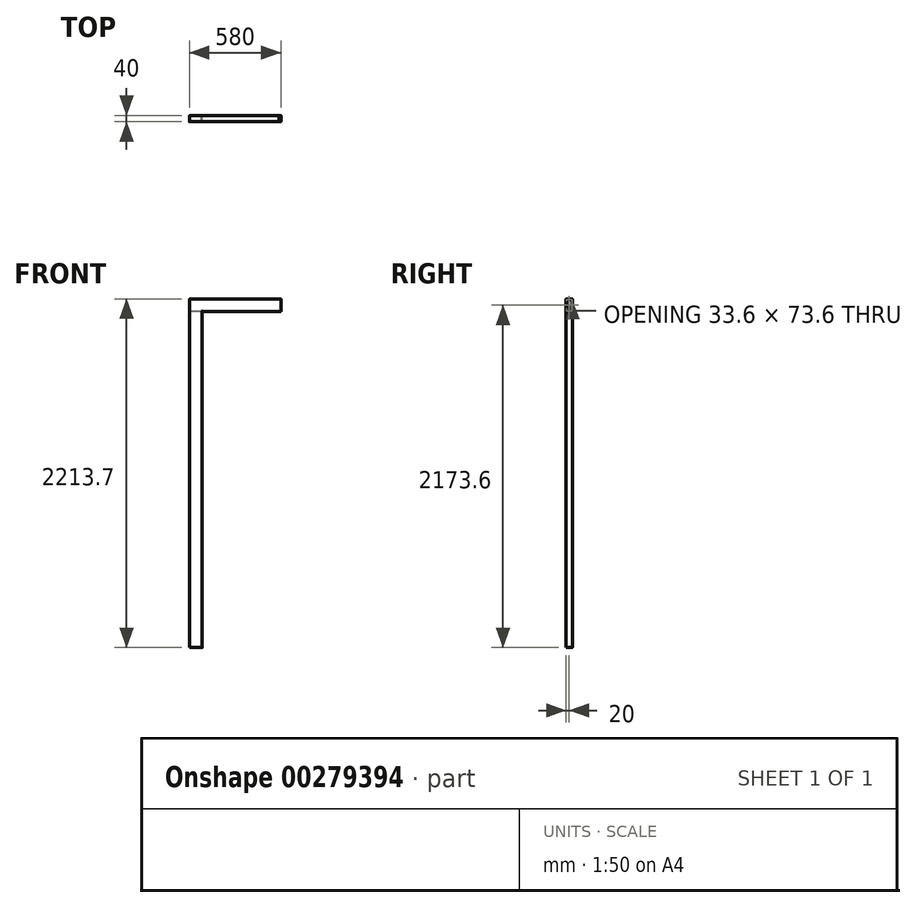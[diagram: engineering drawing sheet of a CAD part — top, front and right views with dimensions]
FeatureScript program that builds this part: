
annotation { "Feature Type Name" : "Feature", "Feature Type Description" : "" }
export const myFeature = defineFeature(function(context is Context, id is Id, definition is map)
    precondition{}
    {
        {
            var Q0;
            Q0=qCreatedBy(makeId("Top.planeOp"),FACE);
            var sketch = newSketch(context, id + "F0", { "sketchPlane" : qUnion([Q0])});
            skLineSegment(sketch, "E0.bottom", {"start": v(40, -20) * mm, "end": v(-40, -20) * mm});
            skLineSegment(sketch, "E0.top", {"start": v(40, 20) * mm, "end": v(-40, 20) * mm});
            skLineSegment(sketch, "E0.left", {"start": v(40, -20) * mm, "end": v(40, 20) * mm});
            skLineSegment(sketch, "E0.right", {"start": v(-40, -20) * mm, "end": v(-40, 20) * mm});
            skPoint(sketch, "E0.middle", {"position": v(0, 0) * mm});
            skLineSegment(sketch, "E1.bottom", {"start": v(34.8, -16.8) * mm, "end": v(-34.8, -16.8) * mm});
            skLineSegment(sketch, "E1.top", {"start": v(34.8, 16.8) * mm, "end": v(-34.8, 16.8) * mm});
            skLineSegment(sketch, "E1.left", {"start": v(36.8, -14.8) * mm, "end": v(36.8, 14.8) * mm});
            skLineSegment(sketch, "E1.right", {"start": v(-36.8, -14.8) * mm, "end": v(-36.8, 14.8) * mm});
            skPoint(sketch, "E2.visualSharp", {"position": v(-36.8, -16.8) * mm});
            skArc(sketch, "E2.filletArc", {"start": v(-36.8, -14.8) * mm, "mid": v(-36.21, -16.21) * mm, "end": v(-34.8, -16.8) * mm});
            skPoint(sketch, "E3.visualSharp", {"position": v(36.8, 16.8) * mm});
            skArc(sketch, "E3.filletArc", {"start": v(36.8, 14.8) * mm, "mid": v(36.21, 16.21) * mm, "end": v(34.8, 16.8) * mm});
            skPoint(sketch, "E4.visualSharp", {"position": v(36.8, -16.8) * mm});
            skArc(sketch, "E4.filletArc", {"start": v(34.8, -16.8) * mm, "mid": v(36.21, -16.21) * mm, "end": v(36.8, -14.8) * mm});
            skPoint(sketch, "E5.visualSharp", {"position": v(-36.8, 16.8) * mm});
            skArc(sketch, "E5.filletArc", {"start": v(-34.8, 16.8) * mm, "mid": v(-36.21, 16.21) * mm, "end": v(-36.8, 14.8) * mm});
            skSolve(sketch);
        }
        {
            var Q0;
            Q0=makeQuery(id+"F0.imprint","IMPRINT",FACE,{"disambiguationData":[TD([[makeQuery(id+"F0.imprint","IMPRINT",EDGE,{"derivedFrom":sQuery(id+"F0.wireOp",EDGE,"E0.bottom")}),-1.0]])]});
            extrude(context, id + "F1", {"entities" : qUnion([Q0]), "depth" : 2133.6 * mm});
        }
        {
            var Q0;
            Q0=makeQuery(id+"F1.opExtrude","CAP_FACE",FACE,{"disambiguationData":[OSD([sQuery(id+"F0.wireOp",EDGE,"E0.bottom"),sQuery(id+"F0.wireOp",EDGE,"E0.top"),sQuery(id+"F0.wireOp",EDGE,"E0.left"),sQuery(id+"F0.wireOp",EDGE,"E0.right"),sQuery(id+"F0.wireOp",EDGE,"E1.bottom"),sQuery(id+"F0.wireOp",EDGE,"E1.top"),sQuery(id+"F0.wireOp",EDGE,"E1.left"),sQuery(id+"F0.wireOp",EDGE,"E1.right"),sQuery(id+"F0.wireOp",EDGE,"E2.filletArc"),sQuery(id+"F0.wireOp",EDGE,"E3.filletArc"),sQuery(id+"F0.wireOp",EDGE,"E4.filletArc"),sQuery(id+"F0.wireOp",EDGE,"E5.filletArc")])],"isStart":false});
            var sketch = newSketch(context, id + "F2", { "sketchPlane" : qUnion([Q0])});
            skLineSegment(sketch, "E6.bottom", {"start": v(-40, -20) * mm, "end": v(40, -20) * mm});
            skLineSegment(sketch, "E6.top", {"start": v(-40, 20) * mm, "end": v(40, 20) * mm});
            skLineSegment(sketch, "E6.left", {"start": v(-40, -20) * mm, "end": v(-40, 20) * mm});
            skLineSegment(sketch, "E6.right", {"start": v(40, -20) * mm, "end": v(40, 20) * mm});
            skSolve(sketch);
        }
        {
            var Q0;
            Q0 = qSketchRegion(id + "F2", true);
            extrude(context, id + "F3", {"entities" : qUnion([Q0]), "operationType" : NewBodyOperationType.ADD, "depth" : 80 * mm});
        }
        {
            var Q0;
            {var subQ0=sQuery(id+"F0.wireOp",EDGE,"E0.left");Q0=makeQuery(id+"F3.boolean.opBoolean","MERGE",FACE,{"derivedFrom":[makeQuery(id+"F1q7NHaxA0HExfM_1.boolean.opBoolean","MERGE",FACE,{"derivedFrom":[makeQuery(id+"F1.opExtrude","SWEPT_FACE",FACE,{"disambiguationData":[OSD([subQ0])]}),makeQuery(id+"F1q7NHaxA0HExfM_1.opExtrude","SWEPT_FACE",FACE,{"disambiguationData":[OSD([subQ0])]})]}),makeQuery(id+"F3.opExtrude","SWEPT_FACE",FACE,{"disambiguationData":[OSD([sQuery(id+"F2.wireOp",EDGE,"E6.right")])]})]});}
            var sketch = newSketch(context, id + "F4", { "sketchPlane" : qUnion([Q0])});
            skLineSegment(sketch, "E7.bottom", {"start": v(-20, 2213.6) * mm, "end": v(20, 2213.6) * mm});
            skLineSegment(sketch, "E7.top", {"start": v(-20, 2133.6) * mm, "end": v(20, 2133.6) * mm});
            skLineSegment(sketch, "E7.left", {"start": v(-20, 2213.6) * mm, "end": v(-20, 2133.6) * mm});
            skLineSegment(sketch, "E7.right", {"start": v(20, 2213.6) * mm, "end": v(20, 2133.6) * mm});
            skLineSegment(sketch, "E8.bottom", {"start": v(-14.8, 2210.4) * mm, "end": v(14.8, 2210.4) * mm});
            skLineSegment(sketch, "E8.top", {"start": v(-14.8, 2136.8) * mm, "end": v(14.8, 2136.8) * mm});
            skLineSegment(sketch, "E8.left", {"start": v(-16.8, 2208.4) * mm, "end": v(-16.8, 2138.8) * mm});
            skLineSegment(sketch, "E8.right", {"start": v(16.8, 2208.4) * mm, "end": v(16.8, 2138.8) * mm});
            skPoint(sketch, "E9.visualSharp", {"position": v(-16.8, 2210.4) * mm});
            skArc(sketch, "E9.filletArc", {"start": v(-14.8, 2210.4) * mm, "mid": v(-16.21, 2209.81) * mm, "end": v(-16.8, 2208.4) * mm});
            skPoint(sketch, "E10.visualSharp", {"position": v(16.8, 2210.4) * mm});
            skArc(sketch, "E10.filletArc", {"start": v(16.8, 2208.4) * mm, "mid": v(16.21, 2209.81) * mm, "end": v(14.8, 2210.4) * mm});
            skPoint(sketch, "E11.visualSharp", {"position": v(16.8, 2136.8) * mm});
            skArc(sketch, "E11.filletArc", {"start": v(14.8, 2136.8) * mm, "mid": v(16.21, 2137.39) * mm, "end": v(16.8, 2138.8) * mm});
            skPoint(sketch, "E12.visualSharp", {"position": v(-16.8, 2136.8) * mm});
            skArc(sketch, "E12.filletArc", {"start": v(-16.8, 2138.8) * mm, "mid": v(-16.21, 2137.39) * mm, "end": v(-14.8, 2136.8) * mm});
            skSolve(sketch);
        }
        {
            var Q0;
            Q0=makeQuery(id+"F4.imprint","IMPRINT",FACE,{"disambiguationData":[TD([[makeQuery(id+"F4.imprint","IMPRINT",EDGE,{"derivedFrom":sQuery(id+"F4.wireOp",EDGE,"E8.bottom")}),-1.0]])]});
            extrude(context, id + "F5", {"entities" : qUnion([Q0]), "operationType" : NewBodyOperationType.REMOVE, "oppositeDirection" : true, "depth" : 100 * mm});
        }
        {
            var Q0;
            Q0 = qSketchRegion(id + "F4", true);
            extrude(context, id + "F6", {"entities" : qUnion([Q0]), "operationType" : NewBodyOperationType.ADD, "depth" : 500 * mm});
        }
        {
            var Q0;
            {var subQ0=sQuery(id+"F0.wireOp",EDGE,"E0.left");var subQ1=sQuery(id+"F0.wireOp",EDGE,"E0.bottom");Q0=makeQuery(id+"F3.boolean.opBoolean","MERGE",EDGE,{"derivedFrom":[makeQuery(id+"F1q7NHaxA0HExfM_1.boolean.opBoolean","MERGE",EDGE,{"derivedFrom":[makeQuery(id+"F1.opExtrude","SWEPT_EDGE",EDGE,{"disambiguationData":[OSD([subQ1,subQ0])]}),makeQuery(id+"F1q7NHaxA0HExfM_1.opExtrude","SWEPT_EDGE",EDGE,{"disambiguationData":[OSD([subQ1,subQ0])]})]}),makeQuery(id+"F3.opExtrude","SWEPT_EDGE",EDGE,{"disambiguationData":[OSD([sQuery(id+"F2.wireOp",EDGE,"E6.bottom"),sQuery(id+"F2.wireOp",EDGE,"E6.right")])]})]});}
            var Q1;
            {var subQ0=sQuery(id+"F0.wireOp",EDGE,"E0.left");var subQ1=sQuery(id+"F0.wireOp",EDGE,"E0.top");Q1=makeQuery(id+"F3.boolean.opBoolean","MERGE",EDGE,{"derivedFrom":[makeQuery(id+"F1q7NHaxA0HExfM_1.boolean.opBoolean","MERGE",EDGE,{"derivedFrom":[makeQuery(id+"F1.opExtrude","SWEPT_EDGE",EDGE,{"disambiguationData":[OSD([subQ1,subQ0])]}),makeQuery(id+"F1q7NHaxA0HExfM_1.opExtrude","SWEPT_EDGE",EDGE,{"disambiguationData":[OSD([subQ1,subQ0])]})]}),makeQuery(id+"F3.opExtrude","SWEPT_EDGE",EDGE,{"disambiguationData":[OSD([sQuery(id+"F2.wireOp",EDGE,"E6.top"),sQuery(id+"F2.wireOp",EDGE,"E6.right")])]})]});}
            var Q2;
            {var subQ0=sQuery(id+"F0.wireOp",EDGE,"E0.right");var subQ1=sQuery(id+"F0.wireOp",EDGE,"E0.bottom");Q2=makeQuery(id+"F3.boolean.opBoolean","MERGE",EDGE,{"derivedFrom":[makeQuery(id+"F1q7NHaxA0HExfM_1.boolean.opBoolean","MERGE",EDGE,{"derivedFrom":[makeQuery(id+"F1.opExtrude","SWEPT_EDGE",EDGE,{"disambiguationData":[OSD([subQ1,subQ0])]}),makeQuery(id+"F1q7NHaxA0HExfM_1.opExtrude","SWEPT_EDGE",EDGE,{"disambiguationData":[OSD([subQ1,subQ0])]})]}),makeQuery(id+"F3.opExtrude","SWEPT_EDGE",EDGE,{"disambiguationData":[OSD([sQuery(id+"F2.wireOp",EDGE,"E6.bottom"),sQuery(id+"F2.wireOp",EDGE,"E6.left")])]})]});}
            var Q3;
            {var subQ0=sQuery(id+"F0.wireOp",EDGE,"E0.right");var subQ1=sQuery(id+"F0.wireOp",EDGE,"E0.top");Q3=makeQuery(id+"F3.boolean.opBoolean","MERGE",EDGE,{"derivedFrom":[makeQuery(id+"F1q7NHaxA0HExfM_1.boolean.opBoolean","MERGE",EDGE,{"derivedFrom":[makeQuery(id+"F1.opExtrude","SWEPT_EDGE",EDGE,{"disambiguationData":[OSD([subQ1,subQ0])]}),makeQuery(id+"F1q7NHaxA0HExfM_1.opExtrude","SWEPT_EDGE",EDGE,{"disambiguationData":[OSD([subQ1,subQ0])]})]}),makeQuery(id+"F3.opExtrude","SWEPT_EDGE",EDGE,{"disambiguationData":[OSD([sQuery(id+"F2.wireOp",EDGE,"E6.top"),sQuery(id+"F2.wireOp",EDGE,"E6.left")])]})]});}
            fillet(context, id + "F7", {"entities" : qUnion([Q0, Q1, Q2, Q3]), "radius" : 2 * mm, "tangentPropagation" : true, "allowEdgeOverflow" : false});
        }
        {
            var Q0;
            Q0=makeQuery(id+"F6.boolean.opBoolean","MERGE",EDGE,{"derivedFrom":[makeQuery(id+"F3.opExtrude","CAP_EDGE",EDGE,{"disambiguationData":[OSD([sQuery(id+"F2.wireOp",EDGE,"E6.bottom")])],"isStart":false}),makeQuery(id+"F6.opExtrude","SWEPT_EDGE",EDGE,{"disambiguationData":[OSD([sQuery(id+"F4.wireOp",EDGE,"E7.bottom"),sQuery(id+"F4.wireOp",EDGE,"E7.left")])]})]});
            var Q1;
            Q1=makeQuery(id+"F6.opExtrude","SWEPT_EDGE",EDGE,{"disambiguationData":[OSD([sQuery(id+"F0.wireOp",EDGE,"E0.bottom"),sQuery(id+"F0.wireOp",EDGE,"E0.left"),sQuery(id+"F2.wireOp",EDGE,"E6.bottom"),sQuery(id+"F2.wireOp",EDGE,"E6.right"),sQuery(id+"F4.wireOp",EDGE,"E7.top"),sQuery(id+"F4.wireOp",EDGE,"E7.left")])]});
            var Q2;
            Q2=makeQuery(id+"F6.opExtrude","SWEPT_EDGE",EDGE,{"disambiguationData":[OSD([sQuery(id+"F0.wireOp",EDGE,"E0.top"),sQuery(id+"F0.wireOp",EDGE,"E0.left"),sQuery(id+"F2.wireOp",EDGE,"E6.top"),sQuery(id+"F2.wireOp",EDGE,"E6.right"),sQuery(id+"F4.wireOp",EDGE,"E7.top"),sQuery(id+"F4.wireOp",EDGE,"E7.right")])]});
            fillet(context, id + "F8", {"entities" : qUnion([Q0, Q1, Q2]), "radius" : 2 * mm, "tangentPropagation" : true, "rho" : 0.5, "crossSection" : FilletCrossSection.CONIC, "allowEdgeOverflow" : false});
        }
        {
            var Q0;
            Q0=makeQuery(id+"F6.boolean.opBoolean","MERGE",FACE,{"derivedFrom":[makeQuery(id+"F3.opExtrude","CAP_FACE",FACE,{"disambiguationData":[OSD([sQuery(id+"F2.wireOp",EDGE,"E6.bottom"),sQuery(id+"F2.wireOp",EDGE,"E6.top"),sQuery(id+"F2.wireOp",EDGE,"E6.left"),sQuery(id+"F2.wireOp",EDGE,"E6.right")])],"isStart":false}),makeQuery(id+"F6.opExtrude","SWEPT_FACE",FACE,{"disambiguationData":[OSD([sQuery(id+"F4.wireOp",EDGE,"E7.bottom")])]})]});
            var sketch = newSketch(context, id + "F9", { "sketchPlane" : qUnion([Q0])});
            skLineSegment(sketch, "E13.bottom", {"start": v(540, 18) * mm, "end": v(530, 18) * mm});
            skLineSegment(sketch, "E13.top", {"start": v(540, -18) * mm, "end": v(530, -18) * mm});
            skLineSegment(sketch, "E13.left", {"start": v(540, 18) * mm, "end": v(540, -18) * mm});
            skLineSegment(sketch, "E13.right", {"start": v(530, 18) * mm, "end": v(530, -18) * mm});
            skSolve(sketch);
        }
        {
            var Q0;
            Q0=makeQuery(id+"F9.imprint","IMPRINT",FACE,{"disambiguationData":[TD([[makeQuery(id+"F9.imprint","IMPRINT",EDGE,{"derivedFrom":sQuery(id+"F9.wireOp",EDGE,"E13.bottom")}),1.0]])]});
            extrude(context, id + "F10", {"entities" : qUnion([Q0]), "operationType" : NewBodyOperationType.ADD, "depth" : .1 * mm});
        }
    });
